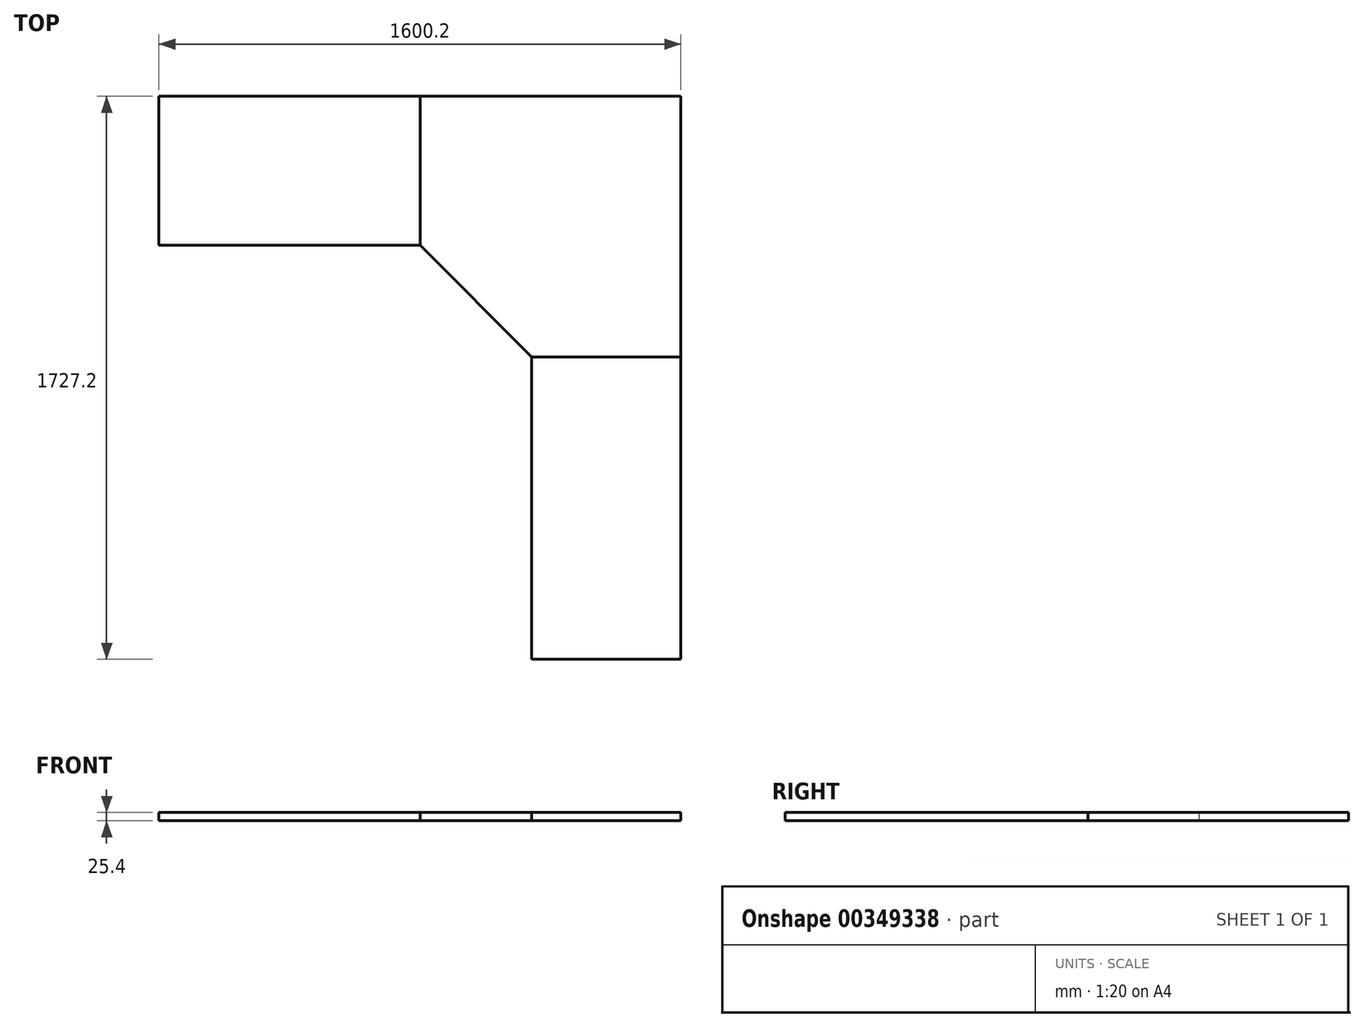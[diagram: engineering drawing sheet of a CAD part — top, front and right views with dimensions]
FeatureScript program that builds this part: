
annotation { "Feature Type Name" : "Feature", "Feature Type Description" : "" }
export const myFeature = defineFeature(function(context is Context, id is Id, definition is map)
    precondition{}
    {
        {
            var Q0;
            Q0=qCreatedBy(makeId("Top.planeOp"),FACE);
            var sketch = newSketch(context, id + "F0", { "sketchPlane" : qUnion([Q0])});
            skLineSegment(sketch, "E0.bottom", {"start": v(-1625.6, 101.6) * mm, "end": v(0, 101.6) * mm});
            skLineSegment(sketch, "E0.top", {"start": v(-1625.6, 0) * mm, "end": v(0, 0) * mm});
            skLineSegment(sketch, "E1.bottom", {"start": v(0, 101.6) * mm, "end": v(101.6, 101.6) * mm});
            skLineSegment(sketch, "E1.top", {"start": v(0, -1752.6) * mm, "end": v(101.6, -1752.6) * mm});
            skLineSegment(sketch, "E1.left", {"start": v(0, 0) * mm, "end": v(0, -1752.6) * mm});
            skLineSegment(sketch, "E1.right", {"start": v(101.6, 101.6) * mm, "end": v(101.6, -1752.6) * mm});
            skLineSegment(sketch, "E2.bottom", {"start": v(-1625.6, 101.6) * mm, "end": v(-1727.2, 101.6) * mm});
            skLineSegment(sketch, "E2.top", {"start": v(-1625.6, -2743.2) * mm, "end": v(-1727.2, -2743.2) * mm});
            skLineSegment(sketch, "E2.left", {"start": v(-1625.6, 0) * mm, "end": v(-1625.6, -2743.2) * mm});
            skLineSegment(sketch, "E2.right", {"start": v(-1727.2, 101.6) * mm, "end": v(-1727.2, -2743.2) * mm});
            skLineSegment(sketch, "E3.bottom", {"start": v(-1625.6, -800.1) * mm, "end": v(-1727.2, -800.1) * mm});
            skLineSegment(sketch, "E3.top", {"start": v(-1625.6, -1562.1) * mm, "end": v(-1727.2, -1562.1) * mm});
            skLineSegment(sketch, "E3.left", {"start": v(-1625.6, -800.1) * mm, "end": v(-1625.6, -1562.1) * mm});
            skLineSegment(sketch, "E3.right", {"start": v(-1727.2, -800.1) * mm, "end": v(-1727.2, -1562.1) * mm});
            skSolve(sketch);
        }
        {
            var Q0;
            Q0=qCreatedBy(makeId("Top.planeOp"),FACE);
            var sketch = newSketch(context, id + "F1", { "sketchPlane" : qUnion([Q0])});
            skLineSegment(sketch, "E4", {"start": v(0, 0) * mm, "end": v(0, -799.96) * mm});
            skLineSegment(sketch, "E5", {"start": v(0, -799.96) * mm, "end": v(-457.2, -799.96) * mm});
            skLineSegment(sketch, "E6", {"start": v(-457.2, -799.96) * mm, "end": v(-799.96, -457.2) * mm});
            skLineSegment(sketch, "E7", {"start": v(-799.96, -457.2) * mm, "end": v(-799.96, 0) * mm});
            skLineSegment(sketch, "E8", {"start": v(-799.96, 0) * mm, "end": v(0, 0) * mm});
            skSolve(sketch);
        }
        {
            var Q0;
            Q0=makeQuery(id+"F0.imprint","IMPRINT",FACE,{"disambiguationData":[TD([[makeQuery(id+"F0.imprint","IMPRINT",EDGE,{"derivedFrom":sQuery(id+"F0.wireOp",EDGE,"E0.bottom")}),-1.0]])]});
            var sketch = newSketch(context, id + "F2", { "sketchPlane" : qUnion([Q0])});
            skLineSegment(sketch, "E9.bottom", {"start": v(-799.96, 0) * mm, "end": v(-1600.2, 0) * mm});
            skLineSegment(sketch, "E9.top", {"start": v(-799.96, -457.2) * mm, "end": v(-1600.2, -457.2) * mm});
            skLineSegment(sketch, "E9.left", {"start": v(-799.96, 0) * mm, "end": v(-799.96, -457.2) * mm});
            skLineSegment(sketch, "E9.right", {"start": v(-1600.2, 0) * mm, "end": v(-1600.2, -457.2) * mm});
            skSolve(sketch);
        }
        {
            var Q0;
            Q0=makeQuery(id+"F1.imprint","IMPRINT",FACE,{"disambiguationData":[TD([[makeQuery(id+"F1.imprint","IMPRINT",EDGE,{"derivedFrom":sQuery(id+"F1.wireOp",EDGE,"E4")}),-1.0]])]});
            var sketch = newSketch(context, id + "F3", { "sketchPlane" : qUnion([Q0])});
            skLineSegment(sketch, "E10.bottom", {"start": v(0, -799.96) * mm, "end": v(-457.2, -799.96) * mm});
            skLineSegment(sketch, "E10.top", {"start": v(0, -1727.2) * mm, "end": v(-457.2, -1727.2) * mm});
            skLineSegment(sketch, "E10.left", {"start": v(0, -799.96) * mm, "end": v(0, -1727.2) * mm});
            skLineSegment(sketch, "E10.right", {"start": v(-457.2, -799.96) * mm, "end": v(-457.2, -1727.2) * mm});
            skSolve(sketch);
        }
        {
            var Q0;
            Q0=makeQuery(id+"F2.imprint","IMPRINT",FACE,{"disambiguationData":[TD([[makeQuery(id+"F2.imprint","IMPRINT",EDGE,{"derivedFrom":sQuery(id+"F2.wireOp",EDGE,"E9.bottom")}),-1.0]])]});
            extrude(context, id + "F4", {"entities" : qUnion([Q0]), "oppositeDirection" : true, "depth" : 25.4 * mm});
        }
        {
            var Q0;
            Q0=makeQuery(id+"F3.imprint","IMPRINT",FACE,{"disambiguationData":[TD([[makeQuery(id+"F3.imprint","IMPRINT",EDGE,{"derivedFrom":sQuery(id+"F3.wireOp",EDGE,"E10.bottom")}),-1.0]])]});
            extrude(context, id + "F5", {"entities" : qUnion([Q0]), "oppositeDirection" : true, "depth" : 25.4 * mm});
        }
        {
            var Q0;
            Q0=makeQuery(id+"F3.imprint","IMPRINT",FACE,{"disambiguationData":[TD([[makeQuery(id+"F3.imprint","IMPRINT",EDGE,{"derivedFrom":sQuery(id+"F3.wireOp",EDGE,"E10.bottom")}),1.0]])]});
            extrude(context, id + "F6", {"entities" : qUnion([Q0]), "oppositeDirection" : true, "depth" : 25.4 * mm});
        }
    });
